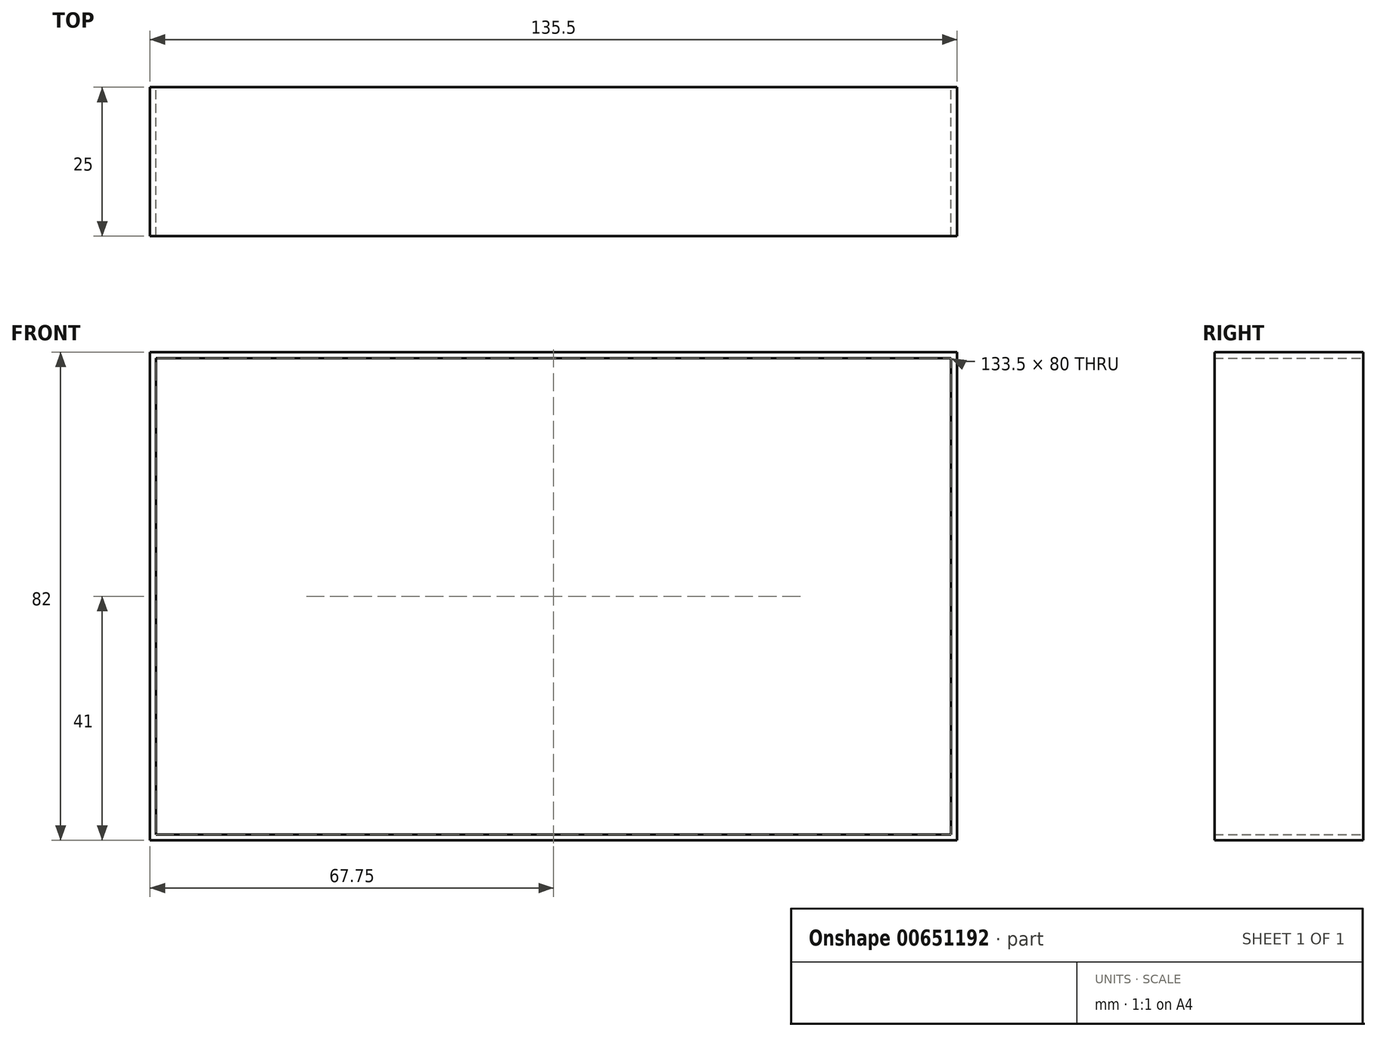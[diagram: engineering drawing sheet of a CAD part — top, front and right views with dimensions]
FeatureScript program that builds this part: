
annotation { "Feature Type Name" : "Feature", "Feature Type Description" : "" }
export const myFeature = defineFeature(function(context is Context, id is Id, definition is map)
    precondition{}
    {
        {
            var Q0;
            Q0=qCreatedBy(makeId("Front.planeOp"),FACE);
            var sketch = newSketch(context, id + "F0", { "sketchPlane" : qUnion([Q0])});
            skLineSegment(sketch, "E0.bottom", {"start": v(67.75, 41) * mm, "end": v(-67.75, 41) * mm});
            skLineSegment(sketch, "E0.top", {"start": v(67.75, -41) * mm, "end": v(-67.75, -41) * mm});
            skLineSegment(sketch, "E0.left", {"start": v(67.75, 41) * mm, "end": v(67.75, -41) * mm});
            skLineSegment(sketch, "E0.right", {"start": v(-67.75, 41) * mm, "end": v(-67.75, -41) * mm});
            skPoint(sketch, "E0.middle", {"position": v(0, 0) * mm});
            skLineSegment(sketch, "E1.bottom", {"start": v(66.75, 40) * mm, "end": v(-66.75, 40) * mm});
            skLineSegment(sketch, "E1.top", {"start": v(66.75, -40) * mm, "end": v(-66.75, -40) * mm});
            skLineSegment(sketch, "E1.left", {"start": v(66.75, 40) * mm, "end": v(66.75, -40) * mm});
            skLineSegment(sketch, "E1.right", {"start": v(-66.75, 40) * mm, "end": v(-66.75, -40) * mm});
            skSolve(sketch);
        }
        {
            var Q0;
            Q0 = qSketchRegion(id + "F0", true);
            extrude(context, id + "F1", {"entities" : qUnion([Q0]), "depth" : 25 * mm, "offsetDistance" : 25 * mm});
        }
    });
